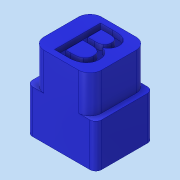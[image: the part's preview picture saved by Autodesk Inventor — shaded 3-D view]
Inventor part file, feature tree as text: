
AUTODESK INVENTOR PART (.ipt)
format: ipt  version: 2018 (Build 220112000, 112)  size: 222,208 bytes
history: native  units: mm
features: sketch x3, extrude x2, fillet x2, other x1, projected_geometry x1
ambient origin geometry x8: Origin, YZ Plane, XZ Plane, XY Plane, X Axis, Y Axis, Z Axis, Center Point
bodies: Volumenkörper1 (feature_tree)
feature tree (9):
  extrude  "Extrusion1"  Depth=10.0mm
  extrude  "Extrusion2"  Depth=10.0mm
  fillet  "Rundung1"  Radius=10.0mm
  fillet  "Rundung2"  Radius=6.5mm
  other  "Prägen1"
  sketch  "Skizze1"  dims[d0=12.0mm d1=10.0mm]
  sketch  "Skizze2"  dims[d2=14.0mm d3=0.0mm d4=10.0mm d5=10.0mm d6=6.5mm d7=0.0mm]
  sketch  "Skizze3"  dims[d8=2.0mm d9=1.0mm d10=1.0mm d11=1.0mm d12=1.0mm d13=3.490659mm]
  projected_geometry  "Projizierte Kontur1"
